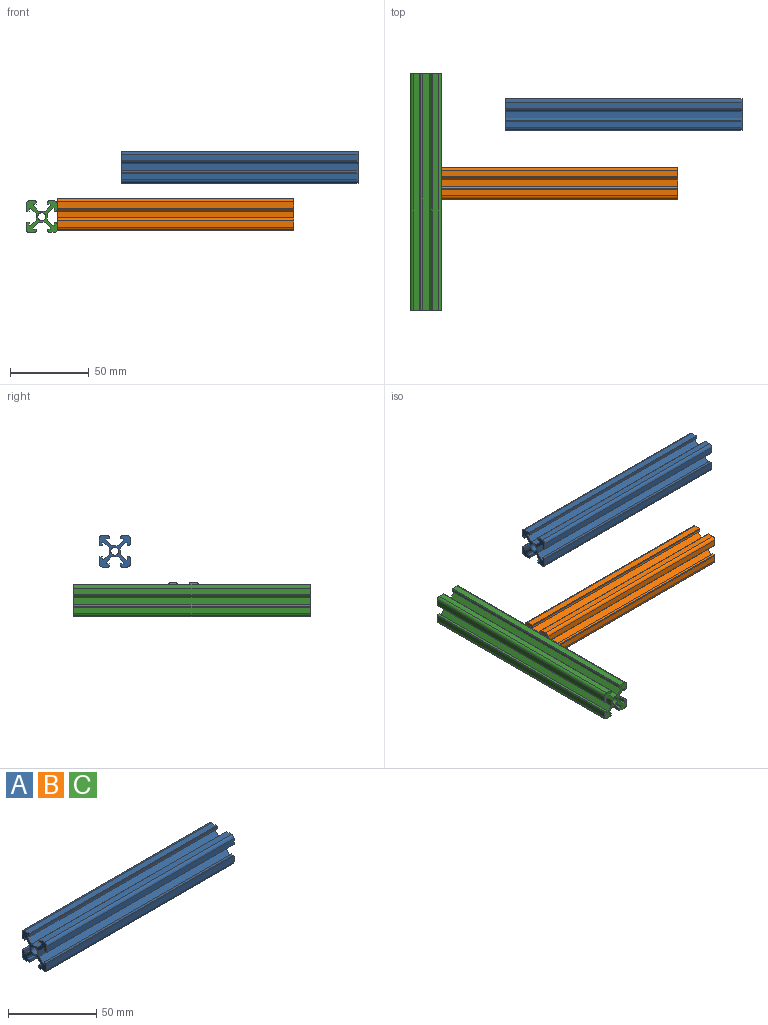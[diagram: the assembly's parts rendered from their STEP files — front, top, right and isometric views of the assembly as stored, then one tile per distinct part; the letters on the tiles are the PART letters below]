
ASSEMBLY  parts=3 mates=1
PART A: 68 faces, bbox 150x20x20 mm
  f0: plane 150x1.5mm, normal (0,1,0), area 225mm2, adj f1,f65,f66,f67
  f1: plane 150x1.9mm, normal (0,0,1), area 285mm2, adj f0,f2,f66,f67
  f2: plane 150x1.09mm, normal (0,1,0), area 162.9mm2, adj f1,f3,f66,f67
  f3: plane 150x3.31mm, normal (0,0.71,-0.71), area 703.1mm2, adj f2,f4,f66,f67
  f4: plane 150x4.37mm, normal (0,0,-1), area 655.7mm2, adj f3,f5,f66,f67
  f5: plane 150x3.31mm, normal (0,-0.71,-0.71), area 703.1mm2, adj f4,f6,f66,f67
  f6: plane 150x1.09mm, normal (0,-1,0), area 162.9mm2, adj f5,f7,f66,f67
  f7: plane 150x1.9mm, normal (0,0,1), area 285mm2, adj f6,f8,f66,f67
  f8: plane 150x1.5mm, normal (0,-1,0), area 225mm2, adj f7,f9,f66,f67
  f9: plane 150x0.5mm, normal (0,0,-1), area 75mm2, adj f8,f10,f66,f67
  f10: plane 150x0.5mm, normal (0,-1,0), area 75mm2, adj f9,f11,f66,f67
  f11: plane 150x3.9mm, normal (0,0,-1), area 585mm2, adj f10,f12,f66,f67
  f12: cylinder r=2mm len=150mm, axis (-1,0,0), area 471.2mm2, adj f11,f13,f66,f67
  f13: plane 150x3.9mm, normal (0,1,0), area 585mm2, adj f12,f14,f66,f67
  f14: plane 150x0.5mm, normal (0,0,1), area 75mm2, adj f13,f15,f66,f67
  f15: plane 150x0.5mm, normal (0,1,0), area 75mm2, adj f14,f16,f66,f67
  f16: plane 150x1.5mm, normal (0,0,1), area 225mm2, adj f15,f17,f66,f67
  f17: plane 150x1.9mm, normal (0,-1,0), area 285mm2, adj f16,f18,f66,f67
  f18: plane 150x1.09mm, normal (0,0,1), area 162.9mm2, adj f17,f19,f66,f67
  f19: plane 150x3.31mm, normal (0,0.71,0.71), area 703.1mm2, adj f18,f20,f66,f67
  f20: plane 150x4.37mm, normal (0,1,0), area 655.7mm2, adj f19,f21,f66,f67
  f21: plane 150x3.31mm, normal (0,0.71,-0.71), area 703.1mm2, adj f20,f22,f66,f67
  f22: plane 150x1.09mm, normal (0,0,-1), area 162.9mm2, adj f21,f23,f66,f67
  f23: plane 150x1.9mm, normal (0,-1,0), area 285mm2, adj f22,f24,f66,f67
  f24: plane 150x1.5mm, normal (0,0,-1), area 225mm2, adj f23,f25,f66,f67
  f25: plane 150x0.5mm, normal (0,1,0), area 75mm2, adj f24,f26,f66,f67
  f26: plane 150x0.5mm, normal (0,0,-1), area 75mm2, adj f25,f27,f66,f67
  f27: plane 150x1.4mm, normal (0,1,0), area 210mm2, adj f26,f28,f66,f67
  f28: plane 150x2.49mm, normal (0,1,0), area 373.9mm2, adj f27,f29,f66,f67
  f29: cylinder r=2mm len=150mm, axis (-1,0,0), area 472.4mm2, adj f28,f30,f66,f67
  f30: plane 150x3.91mm, normal (0,0,1), area 586.4mm2, adj f29,f31,f66,f67
  f31: plane 150x0.5mm, normal (0,-1,0), area 75mm2, adj f30,f32,f66,f67
  f32: plane 150x0.5mm, normal (0,0,1), area 75mm2, adj f31,f33,f66,f67
  f33: plane 150x1.5mm, normal (0,-1,0), area 225mm2, adj f32,f34,f66,f67
  f34: plane 150x1.9mm, normal (0,0,-1), area 285mm2, adj f33,f35,f66,f67
  f35: plane 150x1.09mm, normal (0,-1,0), area 162.9mm2, adj f34,f36,f66,f67
  f36: plane 150x3.31mm, normal (0,-0.71,0.71), area 703.1mm2, adj f35,f37,f66,f67
  f37: plane 150x4.37mm, normal (0,0,1), area 655.7mm2, adj f36,f38,f66,f67
  f38: plane 150x3.31mm, normal (0,0.71,0.71), area 703.1mm2, adj f37,f39,f66,f67
  f39: plane 150x1.09mm, normal (0,1,0), area 162.9mm2, adj f38,f40,f66,f67
  f40: plane 150x1.9mm, normal (0,0,-1), area 285mm2, adj f39,f41,f66,f67
  f41: plane 150x1.5mm, normal (0,1,0), area 225mm2, adj f40,f42,f66,f67
  f42: plane 150x0.5mm, normal (0,0,1), area 75mm2, adj f41,f43,f66,f67
  f43: plane 150x0.5mm, normal (0,1,0), area 75mm2, adj f42,f44,f66,f67
  f44: plane 150x3.9mm, normal (0,0,1), area 585mm2, adj f43,f45,f66,f67
  f45: cylinder r=2mm len=150mm, axis (-1,0,0), area 471.2mm2, adj f44,f46,f66,f67
  f46: plane 150x3.9mm, normal (0,-1,0), area 585mm2, adj f45,f47,f66,f67
  f47: plane 150x0.5mm, normal (0,0,-1), area 75mm2, adj f46,f48,f66,f67
  f48: plane 150x0.5mm, normal (0,-1,0), area 75mm2, adj f47,f49,f66,f67
  f49: plane 150x1.5mm, normal (0,0,-1), area 225mm2, adj f48,f50,f66,f67
  f50: plane 150x1.9mm, normal (0,1,0), area 285mm2, adj f49,f51,f66,f67
  f51: plane 150x1.09mm, normal (0,0,-1), area 162.9mm2, adj f50,f52,f66,f67
  f52: plane 150x3.31mm, normal (0,-0.71,-0.71), area 703.1mm2, adj f51,f53,f66,f67
  f53: plane 150x4.37mm, normal (0,-1,0), area 655.7mm2, adj f52,f54,f66,f67
  f54: plane 150x3.31mm, normal (0,-0.71,0.71), area 703.1mm2, adj f53,f55,f66,f67
  f55: plane 150x1.09mm, normal (0,0,1), area 162.9mm2, adj f54,f56,f66,f67
  f56: plane 150x1.9mm, normal (0,1,0), area 285mm2, adj f55,f57,f66,f67
  f57: plane 150x1.5mm, normal (0,0,1), area 225mm2, adj f56,f58,f66,f67
  f58: plane 150x0.5mm, normal (0,-1,0), area 75mm2, adj f57,f59,f66,f67
  f59: plane 150x0.5mm, normal (0,0,1), area 75mm2, adj f58,f60,f66,f67
  f60: plane 150x3.9mm, normal (0,-1,0), area 585mm2, adj f59,f61,f66,f67
  f61: cylinder r=2mm len=150mm, axis (-1,0,0), area 471.2mm2, adj f60,f62,f66,f67
  f62: plane 150x3.9mm, normal (0,0,-1), area 585mm2, adj f61,f63,f66,f67
  f63: plane 150x0.5mm, normal (0,1,0), area 75mm2, adj f62,f65,f66,f67
  f64: cylinder r=2.5mm len=150mm, axis (-1,0,0), area 2356.2mm2, adj f66,f67
  f65: plane 150x0.5mm, normal (0,0,-1), area 75mm2, adj f0,f63,f66,f67
  f66: plane 20.01x20mm, normal (1,0,0), area 167.7mm2, adj f0,f1,f2,f3,f4,f5,f6,f7
  f67: plane 20.01x20mm, normal (-1,0,0), area 167.7mm2, adj f0,f1,f2,f3,f4,f5,f6,f7
PART B: same geometry as A
PART C: same geometry as A
PLACE A t=(23.4,73.22,24.62)mm
PLACE B t=(-17.3,29.72,-5.38)mm
PLACE C rot(axis=(-0.58,0.58,-0.58),120deg) t=(-27.3,99.22,-6.78)mm
MATE planar C.f30 <-> B.f67  axis (1,0,0) through (-17.3,24.22,-12.83)mm
